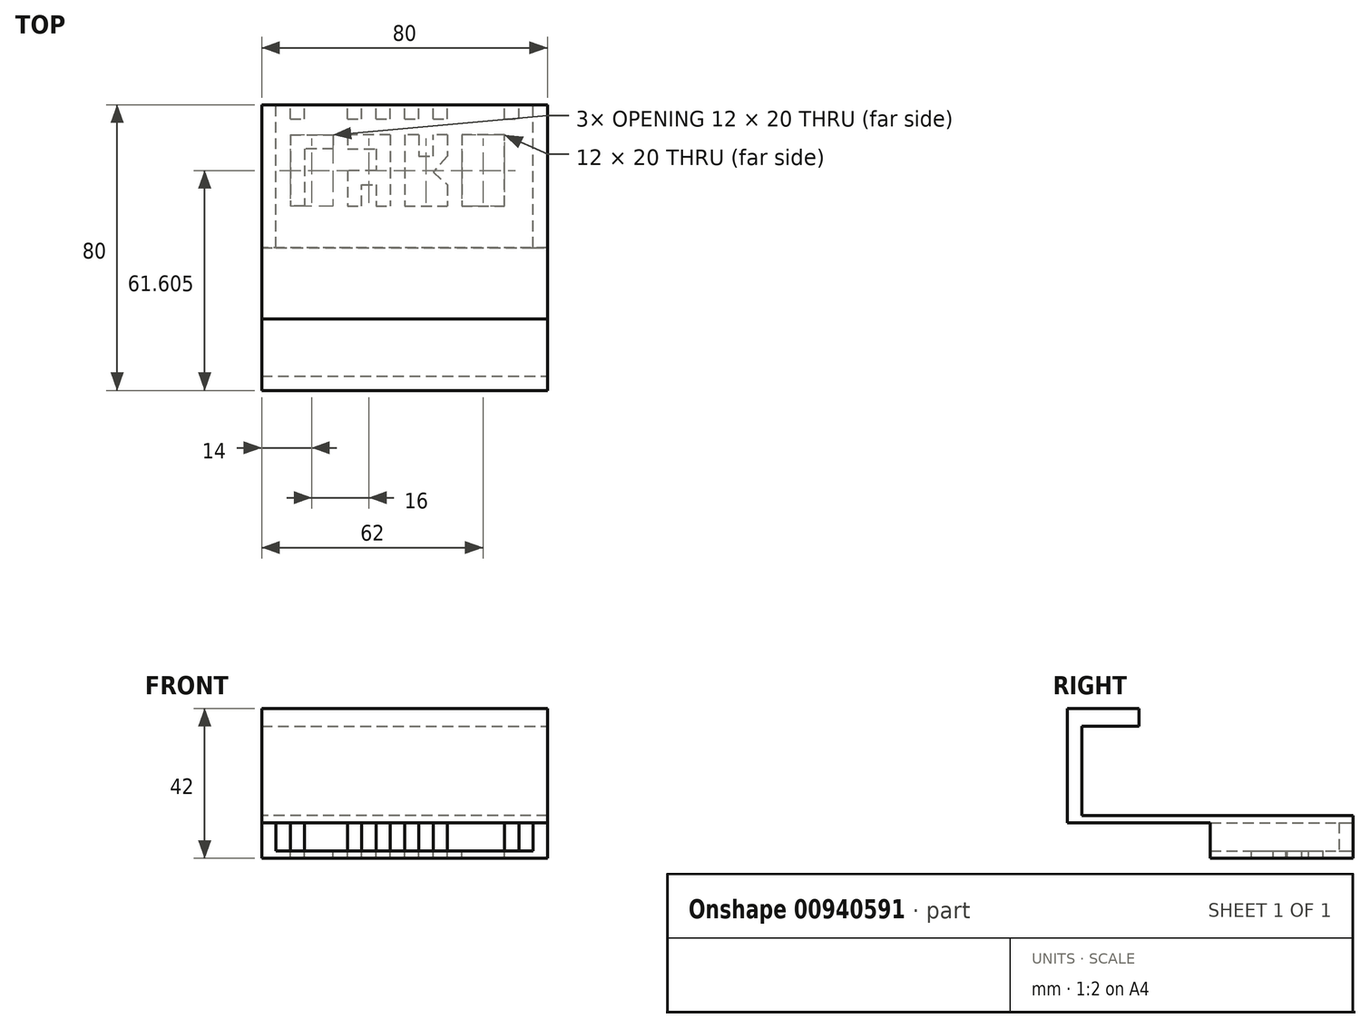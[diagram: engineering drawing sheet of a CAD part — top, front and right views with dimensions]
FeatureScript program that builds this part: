
annotation { "Feature Type Name" : "Feature", "Feature Type Description" : "" }
export const myFeature = defineFeature(function(context is Context, id is Id, definition is map)
    precondition{}
    {
        {
            var Q0;
            Q0=qCreatedBy(makeId("Front.planeOp"),FACE);
            var sketch = newSketch(context, id + "F0", { "sketchPlane" : qUnion([Q0])});
            skLineSegment(sketch, "E0", {"start": v(0, 0) * mm, "end": v(-80, 0) * mm});
            skLineSegment(sketch, "E1", {"start": v(-80, 0) * mm, "end": v(-80, -12) * mm});
            skLineSegment(sketch, "E2", {"start": v(0, -12) * mm, "end": v(0, 0) * mm});
            skLineSegment(sketch, "E3", {"start": v(0, -12) * mm, "end": v(-80, -12) * mm});
            skLineSegment(sketch, "E4", {"start": v(-76, 0) * mm, "end": v(-76, -12) * mm});
            skLineSegment(sketch, "E5", {"start": v(-72, 0) * mm, "end": v(-72, -12) * mm});
            skLineSegment(sketch, "E6", {"start": v(-68, 0) * mm, "end": v(-68, -12) * mm});
            skLineSegment(sketch, "E7", {"start": v(-64, 0) * mm, "end": v(-64, -12) * mm});
            skLineSegment(sketch, "E8", {"start": v(-60, 0) * mm, "end": v(-60, -12) * mm});
            skLineSegment(sketch, "E9", {"start": v(-56, 0) * mm, "end": v(-56, -12) * mm});
            skLineSegment(sketch, "E10", {"start": v(-52, 0) * mm, "end": v(-52, -12) * mm});
            skLineSegment(sketch, "E11", {"start": v(-48, 0) * mm, "end": v(-48, -12) * mm});
            skLineSegment(sketch, "E12", {"start": v(-44, 0) * mm, "end": v(-44, -12) * mm});
            skLineSegment(sketch, "E13", {"start": v(-40, 0) * mm, "end": v(-40, -12) * mm});
            skLineSegment(sketch, "E14", {"start": v(-36, 0) * mm, "end": v(-36, -12) * mm});
            skLineSegment(sketch, "E15", {"start": v(-32, 0) * mm, "end": v(-32, -12) * mm});
            skLineSegment(sketch, "E16", {"start": v(-28, 0) * mm, "end": v(-28, -12) * mm});
            skLineSegment(sketch, "E17", {"start": v(-20, 0) * mm, "end": v(-20, -12) * mm});
            skLineSegment(sketch, "E18", {"start": v(-24, 0) * mm, "end": v(-24, -12) * mm});
            skLineSegment(sketch, "E19", {"start": v(-16, 0) * mm, "end": v(-16, -12) * mm});
            skLineSegment(sketch, "E20", {"start": v(-12, 0) * mm, "end": v(-12, -12) * mm});
            skLineSegment(sketch, "E21", {"start": v(-8, 0) * mm, "end": v(-8, -12) * mm});
            skLineSegment(sketch, "E22", {"start": v(-4, 0) * mm, "end": v(-4, -12) * mm});
            skLineSegment(sketch, "E23", {"start": v(-80, -2) * mm, "end": v(0, -2) * mm});
            skLineSegment(sketch, "E24", {"start": v(-80, -10) * mm, "end": v(0, -10) * mm});
            skSolve(sketch);
        }
        {
            var Q0;
            {var subQ0=sQuery(id+"F0.wireOp",EDGE,"E3");var subQ1=sQuery(id+"F0.wireOp",EDGE,"E1");var subQ2=makeQuery(id+"F0.imprint","INTERSECT",VERTEX,{"derivedFrom":[subQ1,subQ0]});Q0=makeQuery(id+"F0.imprint","IMPRINT",FACE,{"disambiguationData":[TD([[makeQuery(id+"F0.imprint","IMPRINT",EDGE,{"disambiguationData":[TD([[subQ2,1.0]])],"derivedFrom":subQ1}),1.0]])]});}
            var Q1;
            {var subQ0=sQuery(id+"F0.wireOp",EDGE,"E4");var subQ1=sQuery(id+"F0.wireOp",EDGE,"E3");var subQ2=makeQuery(id+"F0.imprint","INTERSECT",VERTEX,{"derivedFrom":[subQ1,subQ0]});Q1=makeQuery(id+"F0.imprint","IMPRINT",FACE,{"disambiguationData":[TD([[makeQuery(id+"F0.imprint","IMPRINT",EDGE,{"disambiguationData":[TD([[subQ2,1.0]])],"derivedFrom":subQ1}),-1.0]])]});}
            var Q2;
            {var subQ0=sQuery(id+"F0.wireOp",EDGE,"E5");var subQ1=sQuery(id+"F0.wireOp",EDGE,"E3");var subQ2=makeQuery(id+"F0.imprint","INTERSECT",VERTEX,{"derivedFrom":[subQ1,subQ0]});Q2=makeQuery(id+"F0.imprint","IMPRINT",FACE,{"disambiguationData":[TD([[makeQuery(id+"F0.imprint","IMPRINT",EDGE,{"disambiguationData":[TD([[subQ2,1.0]])],"derivedFrom":subQ1}),-1.0]])]});}
            var Q3;
            {var subQ0=sQuery(id+"F0.wireOp",EDGE,"E6");var subQ1=sQuery(id+"F0.wireOp",EDGE,"E3");var subQ2=makeQuery(id+"F0.imprint","INTERSECT",VERTEX,{"derivedFrom":[subQ1,subQ0]});Q3=makeQuery(id+"F0.imprint","IMPRINT",FACE,{"disambiguationData":[TD([[makeQuery(id+"F0.imprint","IMPRINT",EDGE,{"disambiguationData":[TD([[subQ2,1.0]])],"derivedFrom":subQ1}),-1.0]])]});}
            var Q4;
            {var subQ0=sQuery(id+"F0.wireOp",EDGE,"E7");var subQ1=sQuery(id+"F0.wireOp",EDGE,"E3");var subQ2=makeQuery(id+"F0.imprint","INTERSECT",VERTEX,{"derivedFrom":[subQ1,subQ0]});Q4=makeQuery(id+"F0.imprint","IMPRINT",FACE,{"disambiguationData":[TD([[makeQuery(id+"F0.imprint","IMPRINT",EDGE,{"disambiguationData":[TD([[subQ2,1.0]])],"derivedFrom":subQ1}),-1.0]])]});}
            var Q5;
            {var subQ0=sQuery(id+"F0.wireOp",EDGE,"E8");var subQ1=sQuery(id+"F0.wireOp",EDGE,"E3");var subQ2=makeQuery(id+"F0.imprint","INTERSECT",VERTEX,{"derivedFrom":[subQ1,subQ0]});Q5=makeQuery(id+"F0.imprint","IMPRINT",FACE,{"disambiguationData":[TD([[makeQuery(id+"F0.imprint","IMPRINT",EDGE,{"disambiguationData":[TD([[subQ2,1.0]])],"derivedFrom":subQ1}),-1.0]])]});}
            var Q6;
            {var subQ0=sQuery(id+"F0.wireOp",EDGE,"E9");var subQ1=sQuery(id+"F0.wireOp",EDGE,"E3");var subQ2=makeQuery(id+"F0.imprint","INTERSECT",VERTEX,{"derivedFrom":[subQ1,subQ0]});Q6=makeQuery(id+"F0.imprint","IMPRINT",FACE,{"disambiguationData":[TD([[makeQuery(id+"F0.imprint","IMPRINT",EDGE,{"disambiguationData":[TD([[subQ2,1.0]])],"derivedFrom":subQ1}),-1.0]])]});}
            var Q7;
            {var subQ0=sQuery(id+"F0.wireOp",EDGE,"E10");var subQ1=sQuery(id+"F0.wireOp",EDGE,"E3");var subQ2=makeQuery(id+"F0.imprint","INTERSECT",VERTEX,{"derivedFrom":[subQ1,subQ0]});Q7=makeQuery(id+"F0.imprint","IMPRINT",FACE,{"disambiguationData":[TD([[makeQuery(id+"F0.imprint","IMPRINT",EDGE,{"disambiguationData":[TD([[subQ2,1.0]])],"derivedFrom":subQ1}),-1.0]])]});}
            var Q8;
            {var subQ0=sQuery(id+"F0.wireOp",EDGE,"E11");var subQ1=sQuery(id+"F0.wireOp",EDGE,"E3");var subQ2=makeQuery(id+"F0.imprint","INTERSECT",VERTEX,{"derivedFrom":[subQ1,subQ0]});Q8=makeQuery(id+"F0.imprint","IMPRINT",FACE,{"disambiguationData":[TD([[makeQuery(id+"F0.imprint","IMPRINT",EDGE,{"disambiguationData":[TD([[subQ2,1.0]])],"derivedFrom":subQ1}),-1.0]])]});}
            var Q9;
            {var subQ0=sQuery(id+"F0.wireOp",EDGE,"E12");var subQ1=sQuery(id+"F0.wireOp",EDGE,"E3");var subQ2=makeQuery(id+"F0.imprint","INTERSECT",VERTEX,{"derivedFrom":[subQ1,subQ0]});Q9=makeQuery(id+"F0.imprint","IMPRINT",FACE,{"disambiguationData":[TD([[makeQuery(id+"F0.imprint","IMPRINT",EDGE,{"disambiguationData":[TD([[subQ2,1.0]])],"derivedFrom":subQ1}),-1.0]])]});}
            var Q10;
            {var subQ0=sQuery(id+"F0.wireOp",EDGE,"E13");var subQ1=sQuery(id+"F0.wireOp",EDGE,"E3");var subQ2=makeQuery(id+"F0.imprint","INTERSECT",VERTEX,{"derivedFrom":[subQ1,subQ0]});Q10=makeQuery(id+"F0.imprint","IMPRINT",FACE,{"disambiguationData":[TD([[makeQuery(id+"F0.imprint","IMPRINT",EDGE,{"disambiguationData":[TD([[subQ2,1.0]])],"derivedFrom":subQ1}),-1.0]])]});}
            var Q11;
            {var subQ0=sQuery(id+"F0.wireOp",EDGE,"E14");var subQ1=sQuery(id+"F0.wireOp",EDGE,"E3");var subQ2=makeQuery(id+"F0.imprint","INTERSECT",VERTEX,{"derivedFrom":[subQ1,subQ0]});Q11=makeQuery(id+"F0.imprint","IMPRINT",FACE,{"disambiguationData":[TD([[makeQuery(id+"F0.imprint","IMPRINT",EDGE,{"disambiguationData":[TD([[subQ2,1.0]])],"derivedFrom":subQ1}),-1.0]])]});}
            var Q12;
            {var subQ0=sQuery(id+"F0.wireOp",EDGE,"E15");var subQ1=sQuery(id+"F0.wireOp",EDGE,"E3");var subQ2=makeQuery(id+"F0.imprint","INTERSECT",VERTEX,{"derivedFrom":[subQ1,subQ0]});Q12=makeQuery(id+"F0.imprint","IMPRINT",FACE,{"disambiguationData":[TD([[makeQuery(id+"F0.imprint","IMPRINT",EDGE,{"disambiguationData":[TD([[subQ2,1.0]])],"derivedFrom":subQ1}),-1.0]])]});}
            var Q13;
            {var subQ0=sQuery(id+"F0.wireOp",EDGE,"E16");var subQ1=sQuery(id+"F0.wireOp",EDGE,"E3");var subQ2=makeQuery(id+"F0.imprint","INTERSECT",VERTEX,{"derivedFrom":[subQ1,subQ0]});Q13=makeQuery(id+"F0.imprint","IMPRINT",FACE,{"disambiguationData":[TD([[makeQuery(id+"F0.imprint","IMPRINT",EDGE,{"disambiguationData":[TD([[subQ2,1.0]])],"derivedFrom":subQ1}),-1.0]])]});}
            var Q14;
            {var subQ0=sQuery(id+"F0.wireOp",EDGE,"E17");var subQ1=sQuery(id+"F0.wireOp",EDGE,"E3");var subQ2=makeQuery(id+"F0.imprint","INTERSECT",VERTEX,{"derivedFrom":[subQ1,subQ0]});Q14=makeQuery(id+"F0.imprint","IMPRINT",FACE,{"disambiguationData":[TD([[makeQuery(id+"F0.imprint","IMPRINT",EDGE,{"disambiguationData":[TD([[subQ2,-1.0]])],"derivedFrom":subQ1}),-1.0]])]});}
            var Q15;
            {var subQ0=sQuery(id+"F0.wireOp",EDGE,"E17");var subQ1=sQuery(id+"F0.wireOp",EDGE,"E3");var subQ2=makeQuery(id+"F0.imprint","INTERSECT",VERTEX,{"derivedFrom":[subQ1,subQ0]});Q15=makeQuery(id+"F0.imprint","IMPRINT",FACE,{"disambiguationData":[TD([[makeQuery(id+"F0.imprint","IMPRINT",EDGE,{"disambiguationData":[TD([[subQ2,1.0]])],"derivedFrom":subQ1}),-1.0]])]});}
            var Q16;
            {var subQ0=sQuery(id+"F0.wireOp",EDGE,"E19");var subQ1=sQuery(id+"F0.wireOp",EDGE,"E3");var subQ2=makeQuery(id+"F0.imprint","INTERSECT",VERTEX,{"derivedFrom":[subQ1,subQ0]});Q16=makeQuery(id+"F0.imprint","IMPRINT",FACE,{"disambiguationData":[TD([[makeQuery(id+"F0.imprint","IMPRINT",EDGE,{"disambiguationData":[TD([[subQ2,1.0]])],"derivedFrom":subQ1}),-1.0]])]});}
            var Q17;
            {var subQ0=sQuery(id+"F0.wireOp",EDGE,"E20");var subQ1=sQuery(id+"F0.wireOp",EDGE,"E3");var subQ2=makeQuery(id+"F0.imprint","INTERSECT",VERTEX,{"derivedFrom":[subQ1,subQ0]});Q17=makeQuery(id+"F0.imprint","IMPRINT",FACE,{"disambiguationData":[TD([[makeQuery(id+"F0.imprint","IMPRINT",EDGE,{"disambiguationData":[TD([[subQ2,1.0]])],"derivedFrom":subQ1}),-1.0]])]});}
            var Q18;
            {var subQ0=sQuery(id+"F0.wireOp",EDGE,"E21");var subQ1=sQuery(id+"F0.wireOp",EDGE,"E3");var subQ2=makeQuery(id+"F0.imprint","INTERSECT",VERTEX,{"derivedFrom":[subQ1,subQ0]});Q18=makeQuery(id+"F0.imprint","IMPRINT",FACE,{"disambiguationData":[TD([[makeQuery(id+"F0.imprint","IMPRINT",EDGE,{"disambiguationData":[TD([[subQ2,1.0]])],"derivedFrom":subQ1}),-1.0]])]});}
            var Q19;
            {var subQ0=sQuery(id+"F0.wireOp",EDGE,"E3");var subQ1=sQuery(id+"F0.wireOp",EDGE,"E2");var subQ2=makeQuery(id+"F0.imprint","INTERSECT",VERTEX,{"derivedFrom":[subQ1,subQ0]});Q19=makeQuery(id+"F0.imprint","IMPRINT",FACE,{"disambiguationData":[TD([[makeQuery(id+"F0.imprint","IMPRINT",EDGE,{"disambiguationData":[TD([[subQ2,-1.0]])],"derivedFrom":subQ1}),1.0]])]});}
            var Q20;
            {var subQ0=sQuery(id+"F0.wireOp",EDGE,"E23");var subQ1=sQuery(id+"F0.wireOp",EDGE,"E1");var subQ2=makeQuery(id+"F0.imprint","INTERSECT",VERTEX,{"derivedFrom":[subQ1,subQ0]});Q20=makeQuery(id+"F0.imprint","IMPRINT",FACE,{"disambiguationData":[TD([[makeQuery(id+"F0.imprint","IMPRINT",EDGE,{"disambiguationData":[TD([[subQ2,-1.0]])],"derivedFrom":subQ1}),1.0]])]});}
            var Q21;
            {var subQ0=sQuery(id+"F0.wireOp",EDGE,"E23");var subQ1=sQuery(id+"F0.wireOp",EDGE,"E2");var subQ2=makeQuery(id+"F0.imprint","INTERSECT",VERTEX,{"derivedFrom":[subQ1,subQ0]});Q21=makeQuery(id+"F0.imprint","IMPRINT",FACE,{"disambiguationData":[TD([[makeQuery(id+"F0.imprint","IMPRINT",EDGE,{"disambiguationData":[TD([[subQ2,1.0]])],"derivedFrom":subQ1}),1.0]])]});}
            extrude(context, id + "F1", {"entities" : qUnion([Q0, Q1, Q2, Q3, Q4, Q5, Q6, Q7, Q8, Q9, Q10, Q11, Q12, Q13, Q14, Q15, Q16, Q17, Q18, Q19, Q20, Q21]), "depth" : 40 * mm, "offsetDistance" : 25 * mm});
        }
        {
            var Q0;
            {var subQ0=sQuery(id+"F0.wireOp",EDGE,"E1");var subQ1=sQuery(id+"F0.wireOp",EDGE,"E0");var subQ2=makeQuery(id+"F0.imprint","INTERSECT",VERTEX,{"derivedFrom":[subQ1,subQ0]});Q0=makeQuery(id+"F0.imprint","IMPRINT",FACE,{"disambiguationData":[TD([[makeQuery(id+"F0.imprint","IMPRINT",EDGE,{"disambiguationData":[TD([[subQ2,1.0]])],"derivedFrom":subQ1}),1.0]])]});}
            var Q1;
            {var subQ0=sQuery(id+"F0.wireOp",EDGE,"E5");var subQ1=sQuery(id+"F0.wireOp",EDGE,"E0");var subQ2=makeQuery(id+"F0.imprint","INTERSECT",VERTEX,{"derivedFrom":[subQ1,subQ0]});Q1=makeQuery(id+"F0.imprint","IMPRINT",FACE,{"disambiguationData":[TD([[makeQuery(id+"F0.imprint","IMPRINT",EDGE,{"disambiguationData":[TD([[subQ2,1.0]])],"derivedFrom":subQ1}),1.0]])]});}
            var Q2;
            {var subQ0=sQuery(id+"F0.wireOp",EDGE,"E4");var subQ1=sQuery(id+"F0.wireOp",EDGE,"E0");var subQ2=makeQuery(id+"F0.imprint","INTERSECT",VERTEX,{"derivedFrom":[subQ1,subQ0]});Q2=makeQuery(id+"F0.imprint","IMPRINT",FACE,{"disambiguationData":[TD([[makeQuery(id+"F0.imprint","IMPRINT",EDGE,{"disambiguationData":[TD([[subQ2,1.0]])],"derivedFrom":subQ1}),1.0]])]});}
            var Q3;
            {var subQ0=sQuery(id+"F0.wireOp",EDGE,"E6");var subQ1=sQuery(id+"F0.wireOp",EDGE,"E0");var subQ2=makeQuery(id+"F0.imprint","INTERSECT",VERTEX,{"derivedFrom":[subQ1,subQ0]});Q3=makeQuery(id+"F0.imprint","IMPRINT",FACE,{"disambiguationData":[TD([[makeQuery(id+"F0.imprint","IMPRINT",EDGE,{"disambiguationData":[TD([[subQ2,1.0]])],"derivedFrom":subQ1}),1.0]])]});}
            var Q4;
            {var subQ0=sQuery(id+"F0.wireOp",EDGE,"E7");var subQ1=sQuery(id+"F0.wireOp",EDGE,"E0");var subQ2=makeQuery(id+"F0.imprint","INTERSECT",VERTEX,{"derivedFrom":[subQ1,subQ0]});Q4=makeQuery(id+"F0.imprint","IMPRINT",FACE,{"disambiguationData":[TD([[makeQuery(id+"F0.imprint","IMPRINT",EDGE,{"disambiguationData":[TD([[subQ2,1.0]])],"derivedFrom":subQ1}),1.0]])]});}
            var Q5;
            {var subQ0=sQuery(id+"F0.wireOp",EDGE,"E8");var subQ1=sQuery(id+"F0.wireOp",EDGE,"E0");var subQ2=makeQuery(id+"F0.imprint","INTERSECT",VERTEX,{"derivedFrom":[subQ1,subQ0]});Q5=makeQuery(id+"F0.imprint","IMPRINT",FACE,{"disambiguationData":[TD([[makeQuery(id+"F0.imprint","IMPRINT",EDGE,{"disambiguationData":[TD([[subQ2,1.0]])],"derivedFrom":subQ1}),1.0]])]});}
            var Q6;
            {var subQ0=sQuery(id+"F0.wireOp",EDGE,"E9");var subQ1=sQuery(id+"F0.wireOp",EDGE,"E0");var subQ2=makeQuery(id+"F0.imprint","INTERSECT",VERTEX,{"derivedFrom":[subQ1,subQ0]});Q6=makeQuery(id+"F0.imprint","IMPRINT",FACE,{"disambiguationData":[TD([[makeQuery(id+"F0.imprint","IMPRINT",EDGE,{"disambiguationData":[TD([[subQ2,1.0]])],"derivedFrom":subQ1}),1.0]])]});}
            var Q7;
            {var subQ0=sQuery(id+"F0.wireOp",EDGE,"E10");var subQ1=sQuery(id+"F0.wireOp",EDGE,"E0");var subQ2=makeQuery(id+"F0.imprint","INTERSECT",VERTEX,{"derivedFrom":[subQ1,subQ0]});Q7=makeQuery(id+"F0.imprint","IMPRINT",FACE,{"disambiguationData":[TD([[makeQuery(id+"F0.imprint","IMPRINT",EDGE,{"disambiguationData":[TD([[subQ2,1.0]])],"derivedFrom":subQ1}),1.0]])]});}
            var Q8;
            {var subQ0=sQuery(id+"F0.wireOp",EDGE,"E11");var subQ1=sQuery(id+"F0.wireOp",EDGE,"E0");var subQ2=makeQuery(id+"F0.imprint","INTERSECT",VERTEX,{"derivedFrom":[subQ1,subQ0]});Q8=makeQuery(id+"F0.imprint","IMPRINT",FACE,{"disambiguationData":[TD([[makeQuery(id+"F0.imprint","IMPRINT",EDGE,{"disambiguationData":[TD([[subQ2,1.0]])],"derivedFrom":subQ1}),1.0]])]});}
            var Q9;
            {var subQ0=sQuery(id+"F0.wireOp",EDGE,"E12");var subQ1=sQuery(id+"F0.wireOp",EDGE,"E0");var subQ2=makeQuery(id+"F0.imprint","INTERSECT",VERTEX,{"derivedFrom":[subQ1,subQ0]});Q9=makeQuery(id+"F0.imprint","IMPRINT",FACE,{"disambiguationData":[TD([[makeQuery(id+"F0.imprint","IMPRINT",EDGE,{"disambiguationData":[TD([[subQ2,1.0]])],"derivedFrom":subQ1}),1.0]])]});}
            var Q10;
            {var subQ0=sQuery(id+"F0.wireOp",EDGE,"E13");var subQ1=sQuery(id+"F0.wireOp",EDGE,"E0");var subQ2=makeQuery(id+"F0.imprint","INTERSECT",VERTEX,{"derivedFrom":[subQ1,subQ0]});Q10=makeQuery(id+"F0.imprint","IMPRINT",FACE,{"disambiguationData":[TD([[makeQuery(id+"F0.imprint","IMPRINT",EDGE,{"disambiguationData":[TD([[subQ2,1.0]])],"derivedFrom":subQ1}),1.0]])]});}
            var Q11;
            {var subQ0=sQuery(id+"F0.wireOp",EDGE,"E14");var subQ1=sQuery(id+"F0.wireOp",EDGE,"E0");var subQ2=makeQuery(id+"F0.imprint","INTERSECT",VERTEX,{"derivedFrom":[subQ1,subQ0]});Q11=makeQuery(id+"F0.imprint","IMPRINT",FACE,{"disambiguationData":[TD([[makeQuery(id+"F0.imprint","IMPRINT",EDGE,{"disambiguationData":[TD([[subQ2,1.0]])],"derivedFrom":subQ1}),1.0]])]});}
            var Q12;
            {var subQ0=sQuery(id+"F0.wireOp",EDGE,"E15");var subQ1=sQuery(id+"F0.wireOp",EDGE,"E0");var subQ2=makeQuery(id+"F0.imprint","INTERSECT",VERTEX,{"derivedFrom":[subQ1,subQ0]});Q12=makeQuery(id+"F0.imprint","IMPRINT",FACE,{"disambiguationData":[TD([[makeQuery(id+"F0.imprint","IMPRINT",EDGE,{"disambiguationData":[TD([[subQ2,1.0]])],"derivedFrom":subQ1}),1.0]])]});}
            var Q13;
            {var subQ0=sQuery(id+"F0.wireOp",EDGE,"E16");var subQ1=sQuery(id+"F0.wireOp",EDGE,"E0");var subQ2=makeQuery(id+"F0.imprint","INTERSECT",VERTEX,{"derivedFrom":[subQ1,subQ0]});Q13=makeQuery(id+"F0.imprint","IMPRINT",FACE,{"disambiguationData":[TD([[makeQuery(id+"F0.imprint","IMPRINT",EDGE,{"disambiguationData":[TD([[subQ2,1.0]])],"derivedFrom":subQ1}),1.0]])]});}
            var Q14;
            {var subQ0=sQuery(id+"F0.wireOp",EDGE,"E17");var subQ1=sQuery(id+"F0.wireOp",EDGE,"E0");var subQ2=makeQuery(id+"F0.imprint","INTERSECT",VERTEX,{"derivedFrom":[subQ1,subQ0]});Q14=makeQuery(id+"F0.imprint","IMPRINT",FACE,{"disambiguationData":[TD([[makeQuery(id+"F0.imprint","IMPRINT",EDGE,{"disambiguationData":[TD([[subQ2,-1.0]])],"derivedFrom":subQ1}),1.0]])]});}
            var Q15;
            {var subQ0=sQuery(id+"F0.wireOp",EDGE,"E17");var subQ1=sQuery(id+"F0.wireOp",EDGE,"E0");var subQ2=makeQuery(id+"F0.imprint","INTERSECT",VERTEX,{"derivedFrom":[subQ1,subQ0]});Q15=makeQuery(id+"F0.imprint","IMPRINT",FACE,{"disambiguationData":[TD([[makeQuery(id+"F0.imprint","IMPRINT",EDGE,{"disambiguationData":[TD([[subQ2,1.0]])],"derivedFrom":subQ1}),1.0]])]});}
            var Q16;
            {var subQ0=sQuery(id+"F0.wireOp",EDGE,"E19");var subQ1=sQuery(id+"F0.wireOp",EDGE,"E0");var subQ2=makeQuery(id+"F0.imprint","INTERSECT",VERTEX,{"derivedFrom":[subQ1,subQ0]});Q16=makeQuery(id+"F0.imprint","IMPRINT",FACE,{"disambiguationData":[TD([[makeQuery(id+"F0.imprint","IMPRINT",EDGE,{"disambiguationData":[TD([[subQ2,1.0]])],"derivedFrom":subQ1}),1.0]])]});}
            var Q17;
            {var subQ0=sQuery(id+"F0.wireOp",EDGE,"E21");var subQ1=sQuery(id+"F0.wireOp",EDGE,"E0");var subQ2=makeQuery(id+"F0.imprint","INTERSECT",VERTEX,{"derivedFrom":[subQ1,subQ0]});Q17=makeQuery(id+"F0.imprint","IMPRINT",FACE,{"disambiguationData":[TD([[makeQuery(id+"F0.imprint","IMPRINT",EDGE,{"disambiguationData":[TD([[subQ2,1.0]])],"derivedFrom":subQ1}),1.0]])]});}
            var Q18;
            {var subQ0=sQuery(id+"F0.wireOp",EDGE,"E2");var subQ1=sQuery(id+"F0.wireOp",EDGE,"E0");var subQ2=makeQuery(id+"F0.imprint","INTERSECT",VERTEX,{"derivedFrom":[subQ1,subQ0]});Q18=makeQuery(id+"F0.imprint","IMPRINT",FACE,{"disambiguationData":[TD([[makeQuery(id+"F0.imprint","IMPRINT",EDGE,{"disambiguationData":[TD([[subQ2,-1.0]])],"derivedFrom":subQ1}),1.0]])]});}
            var Q19;
            {var subQ0=sQuery(id+"F0.wireOp",EDGE,"E20");var subQ1=sQuery(id+"F0.wireOp",EDGE,"E0");var subQ2=makeQuery(id+"F0.imprint","INTERSECT",VERTEX,{"derivedFrom":[subQ1,subQ0]});Q19=makeQuery(id+"F0.imprint","IMPRINT",FACE,{"disambiguationData":[TD([[makeQuery(id+"F0.imprint","IMPRINT",EDGE,{"disambiguationData":[TD([[subQ2,1.0]])],"derivedFrom":subQ1}),1.0]])]});}
            extrude(context, id + "F2", {"entities" : qUnion([Q0, Q1, Q2, Q3, Q4, Q5, Q6, Q7, Q8, Q9, Q10, Q11, Q12, Q13, Q14, Q15, Q16, Q17, Q18, Q19]), "operationType" : NewBodyOperationType.ADD, "depth" : 80 * mm, "offsetDistance" : 25 * mm});
        }
        {
            var Q0;
            Q0=qCreatedBy(makeId("Right.planeOp"),FACE);
            var sketch = newSketch(context, id + "F3", { "sketchPlane" : qUnion([Q0])});
            skLineSegment(sketch, "E25", {"start": v(-80, 0) * mm, "end": v(-80, 30) * mm});
            skLineSegment(sketch, "E26", {"start": v(-80, 30) * mm, "end": v(-60, 30) * mm});
            skLineSegment(sketch, "E27", {"start": v(-76, 0) * mm, "end": v(-76, 25) * mm});
            skLineSegment(sketch, "E28", {"start": v(-76, 25) * mm, "end": v(-60, 25) * mm});
            skLineSegment(sketch, "E29", {"start": v(-60, 25) * mm, "end": v(-60, 30) * mm});
            skLineSegment(sketch, "E30", {"start": v(-80, 0) * mm, "end": v(-76, 0) * mm});
            skSolve(sketch);
        }
        {
            var Q0;
            Q0=makeQuery(id+"F3.imprint","IMPRINT",FACE,{"disambiguationData":[TD([[makeQuery(id+"F3.imprint","IMPRINT",EDGE,{"derivedFrom":sQuery(id+"F3.wireOp",EDGE,"E25")}),-1.0]])]});
            extrude(context, id + "F4", {"entities" : qUnion([Q0]), "operationType" : NewBodyOperationType.ADD, "oppositeDirection" : true, "depth" : 80 * mm, "offsetDistance" : 25 * mm});
        }
        {
            var Q0;
            {var subQ0=sQuery(id+"F0.wireOp",EDGE,"E23");var subQ1=sQuery(id+"F0.wireOp",EDGE,"E5");var subQ2=makeQuery(id+"F0.imprint","INTERSECT",VERTEX,{"derivedFrom":[subQ1,subQ0]});Q0=makeQuery(id+"F0.imprint","IMPRINT",FACE,{"disambiguationData":[TD([[makeQuery(id+"F0.imprint","IMPRINT",EDGE,{"disambiguationData":[TD([[subQ2,-1.0]])],"derivedFrom":subQ1}),1.0]])]});}
            var Q1;
            {var subQ0=sQuery(id+"F0.wireOp",EDGE,"E23");var subQ1=sQuery(id+"F0.wireOp",EDGE,"E9");var subQ2=makeQuery(id+"F0.imprint","INTERSECT",VERTEX,{"derivedFrom":[subQ1,subQ0]});Q1=makeQuery(id+"F0.imprint","IMPRINT",FACE,{"disambiguationData":[TD([[makeQuery(id+"F0.imprint","IMPRINT",EDGE,{"disambiguationData":[TD([[subQ2,-1.0]])],"derivedFrom":subQ1}),1.0]])]});}
            var Q2;
            {var subQ0=sQuery(id+"F0.wireOp",EDGE,"E23");var subQ1=sQuery(id+"F0.wireOp",EDGE,"E11");var subQ2=makeQuery(id+"F0.imprint","INTERSECT",VERTEX,{"derivedFrom":[subQ1,subQ0]});Q2=makeQuery(id+"F0.imprint","IMPRINT",FACE,{"disambiguationData":[TD([[makeQuery(id+"F0.imprint","IMPRINT",EDGE,{"disambiguationData":[TD([[subQ2,-1.0]])],"derivedFrom":subQ1}),1.0]])]});}
            var Q3;
            {var subQ0=sQuery(id+"F0.wireOp",EDGE,"E23");var subQ1=sQuery(id+"F0.wireOp",EDGE,"E13");var subQ2=makeQuery(id+"F0.imprint","INTERSECT",VERTEX,{"derivedFrom":[subQ1,subQ0]});Q3=makeQuery(id+"F0.imprint","IMPRINT",FACE,{"disambiguationData":[TD([[makeQuery(id+"F0.imprint","IMPRINT",EDGE,{"disambiguationData":[TD([[subQ2,-1.0]])],"derivedFrom":subQ1}),1.0]])]});}
            var Q4;
            {var subQ0=sQuery(id+"F0.wireOp",EDGE,"E23");var subQ1=sQuery(id+"F0.wireOp",EDGE,"E15");var subQ2=makeQuery(id+"F0.imprint","INTERSECT",VERTEX,{"derivedFrom":[subQ1,subQ0]});Q4=makeQuery(id+"F0.imprint","IMPRINT",FACE,{"disambiguationData":[TD([[makeQuery(id+"F0.imprint","IMPRINT",EDGE,{"disambiguationData":[TD([[subQ2,-1.0]])],"derivedFrom":subQ1}),1.0]])]});}
            var Q5;
            {var subQ0=sQuery(id+"F0.wireOp",EDGE,"E23");var subQ1=sQuery(id+"F0.wireOp",EDGE,"E20");var subQ2=makeQuery(id+"F0.imprint","INTERSECT",VERTEX,{"derivedFrom":[subQ1,subQ0]});Q5=makeQuery(id+"F0.imprint","IMPRINT",FACE,{"disambiguationData":[TD([[makeQuery(id+"F0.imprint","IMPRINT",EDGE,{"disambiguationData":[TD([[subQ2,-1.0]])],"derivedFrom":subQ1}),1.0]])]});}
            extrude(context, id + "F5", {"entities" : qUnion([Q0, Q1, Q2, Q3, Q4, Q5]), "operationType" : NewBodyOperationType.ADD, "depth" : 4 * mm, "offsetDistance" : 25 * mm});
        }
        {
            var Q0;
            Q0=makeQuery(id+"F2.opExtrude","SWEPT_FACE",FACE,{"disambiguationData":[OSD([sQuery(id+"F0.wireOp",EDGE,"E23")])]});
            var sketch = newSketch(context, id + "F6", { "sketchPlane" : qUnion([Q0])});
            skLineSegment(sketch, "E31", {"start": v(-80, 8.4) * mm, "end": v(0, 8.4) * mm, "construction": true});
            skLineSegment(sketch, "E32", {"start": v(-80, 28.4) * mm, "end": v(0, 28.4) * mm, "construction": true});
            skLineSegment(sketch, "E33", {"start": v(-72, 28.4) * mm, "end": v(-72, 8.4) * mm});
            skLineSegment(sketch, "E34", {"start": v(-68, 28.4) * mm, "end": v(-68, 12.4) * mm});
            skLineSegment(sketch, "E35", {"start": v(-68, 12.4) * mm, "end": v(-60, 12.4) * mm});
            skLineSegment(sketch, "E36", {"start": v(-60, 8.4) * mm, "end": v(-72, 8.4) * mm});
            skLineSegment(sketch, "E37", {"start": v(-60, 12.4) * mm, "end": v(-60, 8.4) * mm});
            skLineSegment(sketch, "E38", {"start": v(-56, 28.4) * mm, "end": v(-56, 18.4) * mm});
            skLineSegment(sketch, "E39", {"start": v(-56, 18.4) * mm, "end": v(-48, 18.4) * mm});
            skLineSegment(sketch, "E40", {"start": v(-48, 18.4) * mm, "end": v(-48, 12.4) * mm});
            skLineSegment(sketch, "E41", {"start": v(-48, 12.4) * mm, "end": v(-56, 12.4) * mm});
            skLineSegment(sketch, "E42", {"start": v(-56, 12.4) * mm, "end": v(-56, 8.4) * mm});
            skLineSegment(sketch, "E43", {"start": v(-56, 8.4) * mm, "end": v(-40, 8.4) * mm});
            skLineSegment(sketch, "E44", {"start": v(-40, 28.4) * mm, "end": v(-48, 28.4) * mm});
            skLineSegment(sketch, "E45", {"start": v(-48, 28.4) * mm, "end": v(-48, 22.4) * mm});
            skLineSegment(sketch, "E46", {"start": v(-48, 22.4) * mm, "end": v(-52, 22.4) * mm});
            skLineSegment(sketch, "E47", {"start": v(-52, 22.4) * mm, "end": v(-52, 28.4) * mm});
            skLineSegment(sketch, "E48", {"start": v(-52, 28.4) * mm, "end": v(-56, 28.4) * mm});
            skLineSegment(sketch, "E49", {"start": v(-40, 28.4) * mm, "end": v(-40, 8.4) * mm});
            skLineSegment(sketch, "E50", {"start": v(-40, 8.4) * mm, "end": v(-36, 8.4) * mm});
            skLineSegment(sketch, "E51", {"start": v(-32, 8.4) * mm, "end": v(-28, 8.4) * mm});
            skLineSegment(sketch, "E52", {"start": v(-28, 28.4) * mm, "end": v(-40, 28.4) * mm});
            skLineSegment(sketch, "E53", {"start": v(-24, 28.4) * mm, "end": v(-24, 8.4) * mm});
            skLineSegment(sketch, "E54", {"start": v(-24, 8.4) * mm, "end": v(-12, 8.4) * mm});
            skLineSegment(sketch, "E55", {"start": v(-12, 8.4) * mm, "end": v(-12, 28.4) * mm});
            skLineSegment(sketch, "E56", {"start": v(-12, 28.4) * mm, "end": v(-24, 28.4) * mm});
            skLineSegment(sketch, "E57", {"start": v(-72, 28.4) * mm, "end": v(-68, 28.4) * mm});
            skLineSegment(sketch, "E58", {"start": v(-44, 28.4) * mm, "end": v(-44, 8.4) * mm});
            skPoint(sketch, "E59", {"position": v(-33.97, 20.4) * mm});
            skLineSegment(sketch, "E60", {"start": v(-40, 28.4) * mm, "end": v(-28, 28.4) * mm});
            skLineSegment(sketch, "E61", {"start": v(-32, 8.4) * mm, "end": v(-32, 14.4) * mm});
            skLineSegment(sketch, "E62", {"start": v(-32, 14.4) * mm, "end": v(-36.03, 14.4) * mm});
            skLineSegment(sketch, "E63", {"start": v(-36.03, 14.4) * mm, "end": v(-36, 8.4) * mm});
            skLineSegment(sketch, "E64", {"start": v(-28, 28.4) * mm, "end": v(-28, 22.4) * mm});
            skLineSegment(sketch, "E65", {"start": v(-28, 22.4) * mm, "end": v(-31.98, 18.78) * mm});
            skLineSegment(sketch, "E66", {"start": v(-31.98, 18.78) * mm, "end": v(-28, 14.4) * mm});
            skLineSegment(sketch, "E67", {"start": v(-28, 14.4) * mm, "end": v(-28, 8.4) * mm});
            skLineSegment(sketch, "E68", {"start": v(-24, 28.4) * mm, "end": v(-12, 28.4) * mm});
            skLineSegment(sketch, "E69", {"start": v(-48, 28.4) * mm, "end": v(-44, 28.4) * mm});
            skLineSegment(sketch, "E70", {"start": v(-56, 28.4) * mm, "end": v(-52, 28.4) * mm});
            skLineSegment(sketch, "E71", {"start": v(-44, 8.4) * mm, "end": v(-56, 8.4) * mm});
            skSolve(sketch);
        }
        {
            var Q0;
            Q0=makeQuery(id+"F6.imprint","IMPRINT",FACE,{"disambiguationData":[TD([[makeQuery(id+"F6.imprint","IMPRINT",EDGE,{"derivedFrom":sQuery(id+"F6.wireOp",EDGE,"E33")}),1.0]])]});
            var Q1;
            Q1=makeQuery(id+"F6.imprint","IMPRINT",FACE,{"disambiguationData":[TD([[makeQuery(id+"F6.imprint","IMPRINT",EDGE,{"derivedFrom":sQuery(id+"F6.wireOp",EDGE,"E53")}),1.0]])]});
            var Q2;
            Q2=makeQuery(id+"F6.imprint","IMPRINT",FACE,{"disambiguationData":[TD([[makeQuery(id+"F6.imprint","IMPRINT",EDGE,{"derivedFrom":sQuery(id+"F6.wireOp",EDGE,"E38")}),1.0]])]});
            var Q3;
            Q3=makeQuery(id+"F6.imprint","IMPRINT",FACE,{"disambiguationData":[TD([[makeQuery(id+"F6.imprint","IMPRINT",EDGE,{"derivedFrom":sQuery(id+"F6.wireOp",EDGE,"E49")}),1.0]])]});
            extrude(context, id + "F7", {"entities" : qUnion([Q0, Q1, Q2, Q3]), "operationType" : NewBodyOperationType.REMOVE, "depth" : 25 * mm, "offsetDistance" : 25 * mm});
        }
    });
